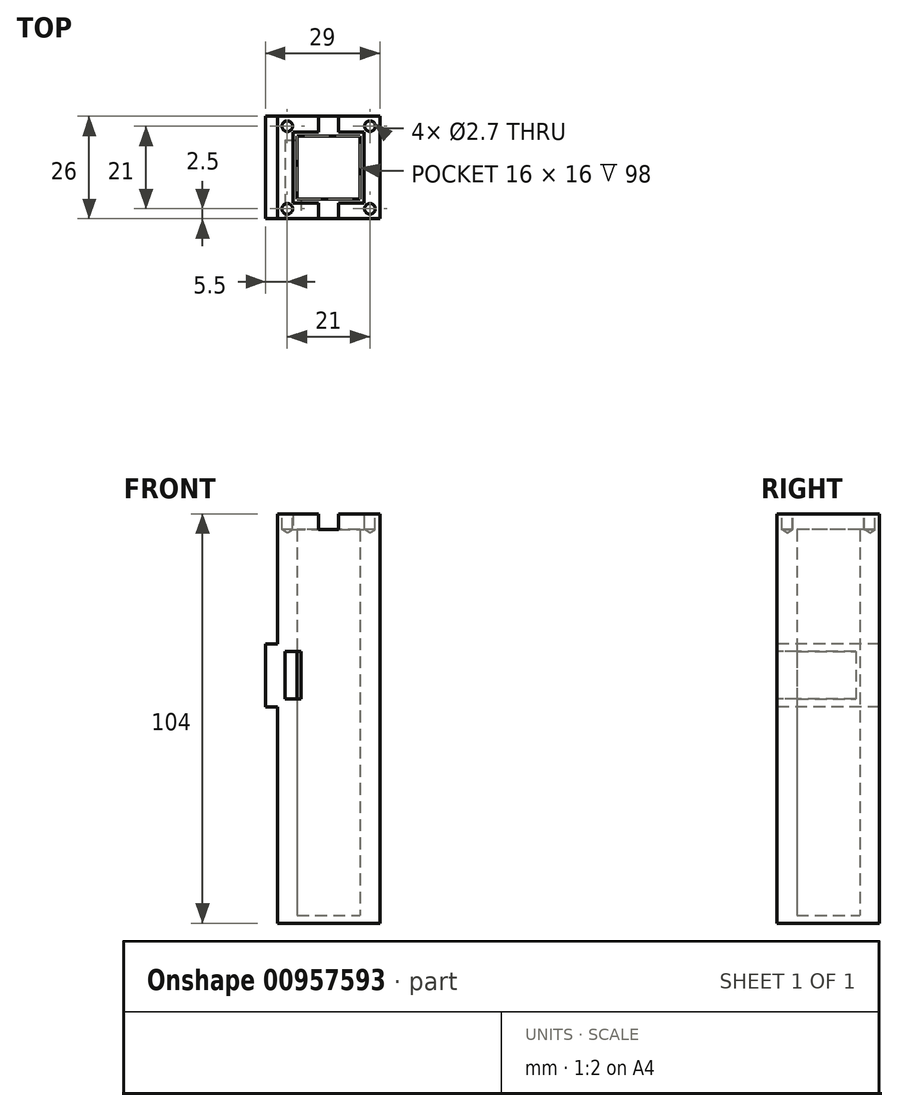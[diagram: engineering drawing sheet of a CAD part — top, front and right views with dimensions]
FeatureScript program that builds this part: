
annotation { "Feature Type Name" : "Feature", "Feature Type Description" : "" }
export const myFeature = defineFeature(function(context is Context, id is Id, definition is map)
    precondition{}
    {
        {
            var Q0;
            Q0=qCreatedBy(makeId("Top.planeOp"),FACE);
            var sketch = newSketch(context, id + "F0", { "sketchPlane" : qUnion([Q0])});
            skLineSegment(sketch, "E0.bottom", {"start": v(13, 13) * mm, "end": v(-13, 13) * mm});
            skLineSegment(sketch, "E0.top", {"start": v(13, -13) * mm, "end": v(-13, -13) * mm});
            skLineSegment(sketch, "E0.left", {"start": v(13, 13) * mm, "end": v(13, -13) * mm});
            skLineSegment(sketch, "E0.right", {"start": v(-13, 13) * mm, "end": v(-13, -13) * mm});
            skPoint(sketch, "E0.middle", {"position": v(0, 0) * mm});
            skLineSegment(sketch, "E1.bottom", {"start": v(8, 8) * mm, "end": v(-8, 8) * mm});
            skLineSegment(sketch, "E1.top", {"start": v(8, -8) * mm, "end": v(-8, -8) * mm});
            skLineSegment(sketch, "E1.left", {"start": v(8, 8) * mm, "end": v(8, -8) * mm});
            skLineSegment(sketch, "E1.right", {"start": v(-8, 8) * mm, "end": v(-8, -8) * mm});
            skSolve(sketch);
        }
        {
            var Q0;
            Q0=makeQuery(id+"F0.imprint","IMPRINT",FACE,{"disambiguationData":[TD([[makeQuery(id+"F0.imprint","IMPRINT",EDGE,{"derivedFrom":sQuery(id+"F0.wireOp",EDGE,"E0.bottom")}),1.0]])]});
            var Q1;
            Q1=makeQuery(id+"F0.imprint","IMPRINT",FACE,{"disambiguationData":[TD([[makeQuery(id+"F0.imprint","IMPRINT",EDGE,{"derivedFrom":sQuery(id+"F0.wireOp",EDGE,"E1.bottom")}),-1.0]])]});
            var Q2;
            Q2=makeQuery(id+"F0.imprint","IMPRINT",FACE,{"disambiguationData":[TD([[makeQuery(id+"F0.imprint","IMPRINT",EDGE,{"derivedFrom":sQuery(id+"F0.wireOp",EDGE,"E1.bottom")}),1.0]])]});
            extrude(context, id + "F1", {"entities" : qUnion([Q0, Q1, Q2]), "depth" : 2 * mm, "offsetDistance" : 25 * mm});
        }
        {
            var Q0;
            Q0=qSketchRegion(id+"F0",true);
            var Q1;
            Q1=makeQuery(id+"F0.imprint","IMPRINT",FACE,{"disambiguationData":[TD([[makeQuery(id+"F0.imprint","IMPRINT",EDGE,{"derivedFrom":sQuery(id+"F0.wireOp",EDGE,"E1.bottom")}),-1.0]])]});
            extrude(context, id + "F2", {"entities" : qUnion([Q0, Q1]), "operationType" : NewBodyOperationType.ADD, "depth" : 100 * mm, "offsetDistance" : 25 * mm});
        }
        {
            var Q0;
            Q0=makeQuery(id+"F2.opExtrude","CAP_FACE",FACE,{"disambiguationData":[OSD([sQuery(id+"F0.wireOp",EDGE,"E0.bottom"),sQuery(id+"F0.wireOp",EDGE,"E0.top"),sQuery(id+"F0.wireOp",EDGE,"E0.left"),sQuery(id+"F0.wireOp",EDGE,"E0.right"),sQuery(id+"F0.wireOp",EDGE,"E1.bottom"),sQuery(id+"F0.wireOp",EDGE,"E1.top"),sQuery(id+"F0.wireOp",EDGE,"E1.left"),sQuery(id+"F0.wireOp",EDGE,"E1.right")])],"isStart":false});
            var sketch = newSketch(context, id + "F3", { "sketchPlane" : qUnion([Q0])});
            skLineSegment(sketch, "E2.bottom", {"start": v(-9, 9) * mm, "end": v(9, 9) * mm});
            skLineSegment(sketch, "E2.top", {"start": v(-9, -9) * mm, "end": v(9, -9) * mm});
            skLineSegment(sketch, "E2.left", {"start": v(-9, 9) * mm, "end": v(-9, -9) * mm});
            skLineSegment(sketch, "E2.right", {"start": v(9, 9) * mm, "end": v(9, -9) * mm});
            skPoint(sketch, "E2.middle", {"position": v(0, 0) * mm});
            skSolve(sketch);
        }
        {
            var Q0;
            Q0=makeQuery(id+"F3.imprint","IMPRINT",FACE,{"disambiguationData":[TD([[makeQuery(id+"F3.imprint","IMPRINT",EDGE,{"derivedFrom":sQuery(id+"F3.wireOp",EDGE,"E2.bottom")}),1.0]])]});
            extrude(context, id + "F4", {"entities" : qUnion([Q0]), "operationType" : NewBodyOperationType.ADD, "depth" : 4 * mm, "offsetDistance" : 25 * mm});
        }
        {
            var Q0;
            Q0=makeQuery(id+"F4.opExtrude","CAP_FACE",FACE,{"disambiguationData":[OSD([sQuery(id+"F0.wireOp",EDGE,"E0.bottom"),sQuery(id+"F0.wireOp",EDGE,"E0.top"),sQuery(id+"F0.wireOp",EDGE,"E0.left"),sQuery(id+"F0.wireOp",EDGE,"E0.right"),sQuery(id+"F3.wireOp",EDGE,"E2.bottom"),sQuery(id+"F3.wireOp",EDGE,"E2.top"),sQuery(id+"F3.wireOp",EDGE,"E2.left"),sQuery(id+"F3.wireOp",EDGE,"E2.right")])],"isStart":false});
            var sketch = newSketch(context, id + "F5", { "sketchPlane" : qUnion([Q0])});
            skLineSegment(sketch, "E3", {"start": v(-2.5, 13) * mm, "end": v(-2.5, 9) * mm});
            skLineSegment(sketch, "E4.MirrorCS", {"start": v(2.5, 13) * mm, "end": v(2.5, 9) * mm});
            skLineSegment(sketch, "E5.MirrorCS", {"start": v(2.5, -13) * mm, "end": v(2.5, -9) * mm});
            skLineSegment(sketch, "E6.MirrorCS", {"start": v(-2.5, -13) * mm, "end": v(-2.5, -9) * mm});
            skLineSegment(sketch, "E7", {"start": v(-13, 13) * mm, "end": v(-9, 9) * mm, "construction": true});
            skPoint(sketch, "E8", {"position": v(-10.5, 10.5) * mm});
            skPoint(sketch, "E9.MirrorP", {"position": v(10.5, 10.5) * mm});
            skLineSegment(sketch, "E10.MirrorCS", {"start": v(13, 13) * mm, "end": v(9, 9) * mm, "construction": true});
            skLineSegment(sketch, "E11.MirrorCS", {"start": v(-13, -13) * mm, "end": v(-9, -9) * mm, "construction": true});
            skPoint(sketch, "E12.MirrorP", {"position": v(-10.5, -10.5) * mm});
            skLineSegment(sketch, "E13.MirrorCS", {"start": v(13, -13) * mm, "end": v(9, -9) * mm, "construction": true});
            skPoint(sketch, "E14.MirrorP", {"position": v(10.5, -10.5) * mm});
            skSolve(sketch);
        }
        {
            var Q0;
            {var subQ0=sQuery(id+"F5.wireOp",EDGE,"E5.MirrorCS");Q0=makeQuery(id+"F5.imprint","IMPRINT",FACE,{"disambiguationData":[TD([[makeQuery(id+"F5.imprint","IMPRINT",EDGE,{"derivedFrom":subQ0}),1.0]])]});}
            var Q1;
            {var subQ0=sQuery(id+"F5.wireOp",EDGE,"E3");Q1=makeQuery(id+"F5.imprint","IMPRINT",FACE,{"disambiguationData":[TD([[makeQuery(id+"F5.imprint","IMPRINT",EDGE,{"derivedFrom":subQ0}),1.0]])]});}
            var Q2;
            Q2=makeQuery(id+"F2.opExtrude","CAP_FACE",FACE,{"disambiguationData":[OSD([sQuery(id+"F0.wireOp",EDGE,"E0.bottom"),sQuery(id+"F0.wireOp",EDGE,"E0.top"),sQuery(id+"F0.wireOp",EDGE,"E0.left"),sQuery(id+"F0.wireOp",EDGE,"E0.right"),sQuery(id+"F0.wireOp",EDGE,"E1.bottom"),sQuery(id+"F0.wireOp",EDGE,"E1.top"),sQuery(id+"F0.wireOp",EDGE,"E1.left"),sQuery(id+"F0.wireOp",EDGE,"E1.right")])],"isStart":false});
            extrude(context, id + "F6", {"entities" : qUnion([Q0, Q1]), "operationType" : NewBodyOperationType.REMOVE, "endBound" : BoundingType.UP_TO_SURFACE, "oppositeDirection" : true, "depth" : 25 * mm, "endBoundEntityFace" : qUnion([Q2]), "offsetDistance" : 25 * mm});
        }
        {
            var Q0;
            Q0=sQuery(id+"F5.wireOp",VERTEX,"E8");
            var Q1;
            Q1=sQuery(id+"F5.wireOp",VERTEX,"E9.MirrorP");
            var Q2;
            Q2=sQuery(id+"F5.wireOp",VERTEX,"E12.MirrorP");
            var Q3;
            Q3=sQuery(id+"F5.wireOp",VERTEX,"E14.MirrorP");
            var Q4;
            Q4=makeQuery(id+"F1.opExtrude","SWEPT_BODY",BODY,{"disambiguationData":[OSD([sQuery(id+"F0.wireOp",EDGE,"E0.bottom"),sQuery(id+"F0.wireOp",EDGE,"E0.top"),sQuery(id+"F0.wireOp",EDGE,"E0.left"),sQuery(id+"F0.wireOp",EDGE,"E0.right")])]});
            hole(context, id + "F7", {"style" : HoleStyle.SIMPLE, "endStyle" : HoleEndStyle.BLIND, "standardTappedOrClearance" : lookupTablePath({ "standard" : "ISO", "engagement" : "50%", "pitch" : "0.5 mm", "size" : "M3", "type" : "Tapped" }), "standardBlindInLast" : lookupTablePath({ "standard" : "ISO", "fit" : "Normal", "engagement" : "50%", "pitch" : "0.5 mm", "size" : "M3", "type" : "Clearance & tapped" }), "holeDiameter" : 2.7 * mm, "majorDiameter" : 3 * mm, "showTappedDepth" : true, "holeDepth" : 4 * mm, "isTappedThrough" : true, "tappedDepth" : 2.5 * mm, "tapClearance" : 3, "locations" : qUnion([Q0, Q1, Q2, Q3]), "scope" : qUnion([Q4])});
        }
        {
            var Q0;
            {var subQ0=sQuery(id+"F0.wireOp",EDGE,"E0.left");Q0=makeQuery(id+"F4.boolean.opBoolean","MERGE",FACE,{"derivedFrom":[makeQuery(id+"F2.boolean.opBoolean","MERGE",FACE,{"derivedFrom":[makeQuery(id+"F1.opExtrude","SWEPT_FACE",FACE,{"disambiguationData":[OSD([subQ0])]}),makeQuery(id+"F2.opExtrude","SWEPT_FACE",FACE,{"disambiguationData":[OSD([subQ0])]})]}),makeQuery(id+"F4.opExtrude","SWEPT_FACE",FACE,{"disambiguationData":[OSD([subQ0])]})]});}
            var sketch = newSketch(context, id + "F8", { "sketchPlane" : qUnion([Q0])});
            skLineSegment(sketch, "E15.bottom", {"start": v(-7.98, 98) * mm, "end": v(8.02, 98) * mm});
            skLineSegment(sketch, "E15.top", {"start": v(-7.98, 2) * mm, "end": v(8.02, 2) * mm});
            skLineSegment(sketch, "E15.left", {"start": v(-7.98, 98) * mm, "end": v(-7.98, 2) * mm});
            skLineSegment(sketch, "E15.right", {"start": v(8.02, 98) * mm, "end": v(8.02, 2) * mm});
            skLineSegment(sketch, "E16", {"start": v(-7.98, 0) * mm, "end": v(-7.98, 100) * mm, "construction": true});
            skLineSegment(sketch, "E17", {"start": v(8.02, 0) * mm, "end": v(8.02, 100) * mm, "construction": true});
            skSolve(sketch);
        }
        {
            var Q0;
            {var subQ0=sQuery(id+"F0.wireOp",EDGE,"E0.top");Q0=makeQuery(id+"F4.boolean.opBoolean","MERGE",FACE,{"derivedFrom":[makeQuery(id+"F2.boolean.opBoolean","MERGE",FACE,{"derivedFrom":[makeQuery(id+"F1.opExtrude","SWEPT_FACE",FACE,{"disambiguationData":[OSD([subQ0])]}),makeQuery(id+"F2.opExtrude","SWEPT_FACE",FACE,{"disambiguationData":[OSD([subQ0])]})]}),makeQuery(id+"F4.opExtrude","SWEPT_FACE",FACE,{"disambiguationData":[OSD([subQ0])]})]});}
            var sketch = newSketch(context, id + "F9", { "sketchPlane" : qUnion([Q0])});
            skLineSegment(sketch, "E18.bottom", {"start": v(-13, 55) * mm, "end": v(-16, 55) * mm});
            skLineSegment(sketch, "E18.top", {"start": v(-13, 71) * mm, "end": v(-16, 71) * mm});
            skLineSegment(sketch, "E18.left", {"start": v(-13, 71) * mm, "end": v(-13, 55) * mm});
            skLineSegment(sketch, "E18.right", {"start": v(-16, 71) * mm, "end": v(-16, 55) * mm});
            skSolve(sketch);
        }
        {
            var Q0;
            Q0 = qSketchRegion(id + "F9", true);
            extrude(context, id + "F10", {"entities" : qUnion([Q0]), "operationType" : NewBodyOperationType.ADD, "oppositeDirection" : true, "depth" : 26 * mm, "offsetDistance" : 25 * mm});
        }
        {
            var Q0;
            {var subQ0=sQuery(id+"F0.wireOp",EDGE,"E0.top");Q0=makeQuery(id+"F10.boolean.opBoolean","MERGE",FACE,{"derivedFrom":[makeQuery(id+"F4.boolean.opBoolean","MERGE",FACE,{"derivedFrom":[makeQuery(id+"F2.boolean.opBoolean","MERGE",FACE,{"derivedFrom":[makeQuery(id+"F1.opExtrude","SWEPT_FACE",FACE,{"disambiguationData":[OSD([subQ0])]}),makeQuery(id+"F2.opExtrude","SWEPT_FACE",FACE,{"disambiguationData":[OSD([subQ0])]})]}),makeQuery(id+"F4.opExtrude","SWEPT_FACE",FACE,{"disambiguationData":[OSD([subQ0])]})]}),makeQuery(id+"F10.opExtrude","CAP_FACE",FACE,{"disambiguationData":[OSD([sQuery(id+"F9.wireOp",EDGE,"E18.bottom"),sQuery(id+"F9.wireOp",EDGE,"E18.top"),sQuery(id+"F9.wireOp",EDGE,"E18.left"),sQuery(id+"F9.wireOp",EDGE,"E18.right")])],"isStart":true})]});}
            var sketch = newSketch(context, id + "F11", { "sketchPlane" : qUnion([Q0])});
            skLineSegment(sketch, "E19.bottom", {"start": v(-11, 69) * mm, "end": v(-7, 69) * mm});
            skLineSegment(sketch, "E19.top", {"start": v(-11, 57) * mm, "end": v(-7, 57) * mm});
            skLineSegment(sketch, "E19.left", {"start": v(-11, 69) * mm, "end": v(-11, 57) * mm});
            skLineSegment(sketch, "E19.right", {"start": v(-7, 69) * mm, "end": v(-7, 57) * mm});
            skSolve(sketch);
        }
        {
            var Q0;
            Q0 = qSketchRegion(id + "F11", true);
            extrude(context, id + "F12", {"entities" : qUnion([Q0]), "operationType" : NewBodyOperationType.REMOVE, "oppositeDirection" : true, "depth" : 20 * mm, "offsetDistance" : 25 * mm});
        }
    });
